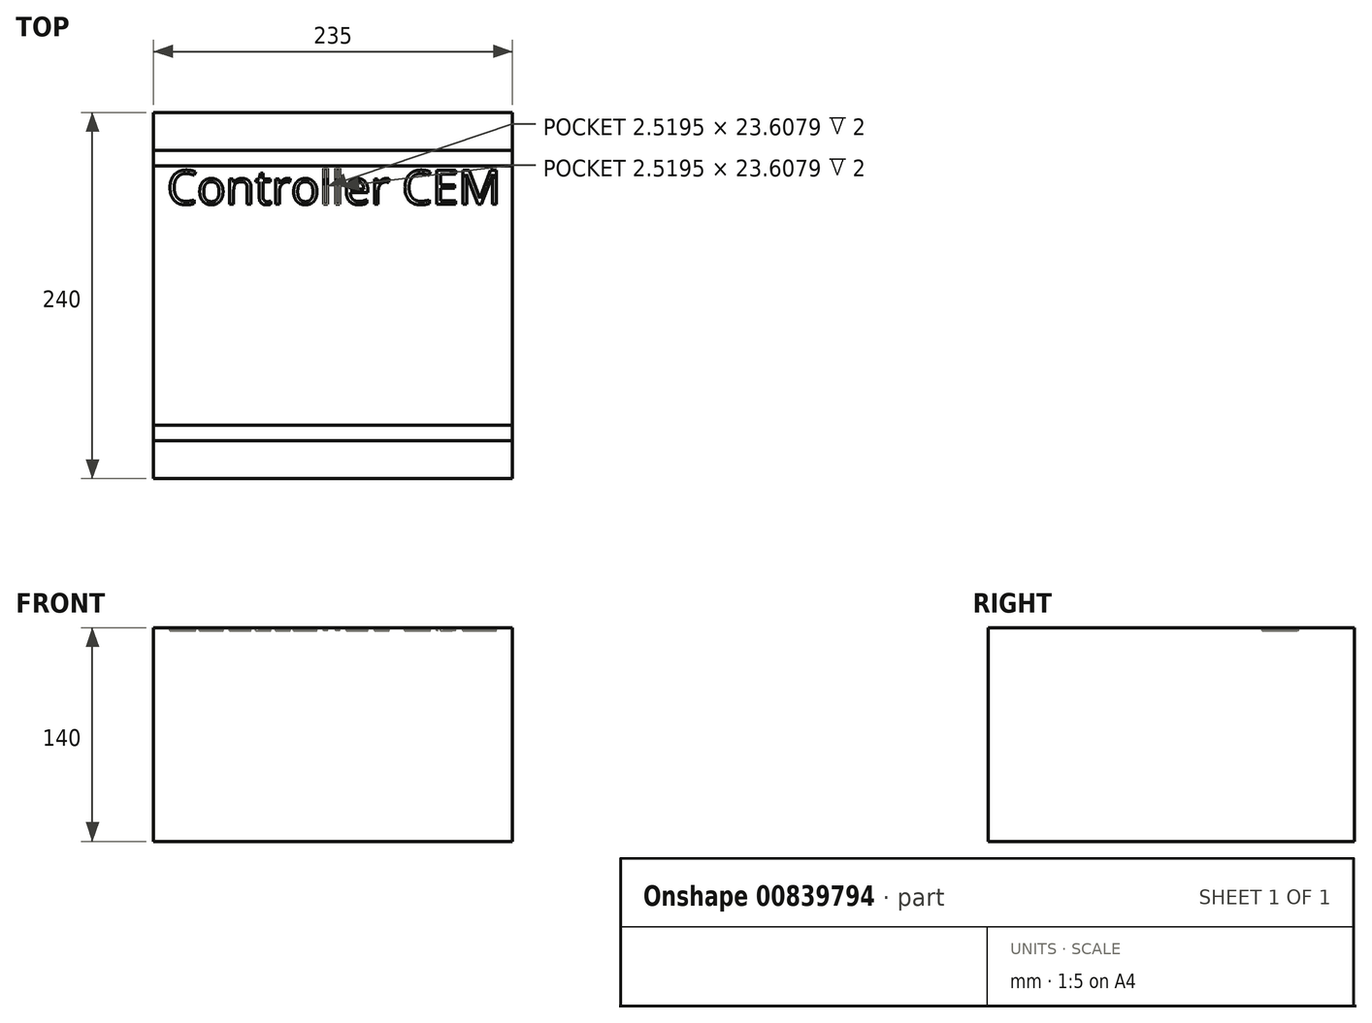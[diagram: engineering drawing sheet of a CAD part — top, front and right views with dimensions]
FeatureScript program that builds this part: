
annotation { "Feature Type Name" : "Feature", "Feature Type Description" : "" }
export const myFeature = defineFeature(function(context is Context, id is Id, definition is map)
    precondition{}
    {
        {
            var Q0;
            Q0=qCreatedBy(makeId("Top.planeOp"),FACE);
            var sketch = newSketch(context, id + "F0", { "sketchPlane" : qUnion([Q0])});
            skLineSegment(sketch, "E0.bottom", {"start": v(-117.5, 120) * mm, "end": v(117.5, 120) * mm});
            skLineSegment(sketch, "E0.top", {"start": v(-117.5, -120) * mm, "end": v(117.5, -120) * mm});
            skLineSegment(sketch, "E0.left", {"start": v(-117.5, 120) * mm, "end": v(-117.5, -120) * mm});
            skLineSegment(sketch, "E0.right", {"start": v(117.5, 120) * mm, "end": v(117.5, -120) * mm});
            skPoint(sketch, "E0.middle", {"position": v(0, 0) * mm});
            skSolve(sketch);
        }
        {
            var Q0;
            Q0 = qSketchRegion(id + "F0", true);
            extrude(context, id + "F1", {"entities" : qUnion([Q0]), "depth" : 140 * mm, "offsetDistance" : 25 * mm});
        }
        {
            var Q0;
            Q0=makeQuery(id+"F1.opExtrude","CAP_FACE",FACE,{"disambiguationData":[OSD([sQuery(id+"F0.wireOp",EDGE,"E0.bottom"),sQuery(id+"F0.wireOp",EDGE,"E0.top"),sQuery(id+"F0.wireOp",EDGE,"E0.left"),sQuery(id+"F0.wireOp",EDGE,"E0.right")])],"isStart":false});
            var sketch = newSketch(context, id + "F2", { "sketchPlane" : qUnion([Q0])});
            skText(sketch, "E1", { "text": "Controller CEM", "fontName": "OpenSans-Regular.ttf"});
            const initialGuessF2  = {"E1": [-0.10864, 0.05975, 1, 0, 0.02237]};
            skSetInitialGuess(sketch, initialGuessF2);
            skSolve(sketch);
        }
        {
            var Q0;
            Q0 = qSketchRegion(id + "F2", true);
            extrude(context, id + "F3", {"entities" : qUnion([Q0]), "operationType" : NewBodyOperationType.REMOVE, "oppositeDirection" : true, "depth" : 2 * mm, "offsetDistance" : 25 * mm});
        }
        {
            var Q0;
            {var subQ0=sQuery(id+"F0.wireOp",EDGE,"E0.top");var subQ1=sQuery(id+"F0.wireOp",EDGE,"E0.right");var subQ2=sQuery(id+"F0.wireOp",EDGE,"E0.bottom");var subQ3=sQuery(id+"F0.wireOp",EDGE,"E0.left");Q0=makeQuery(id+"F3.boolean.opBoolean","SPLIT",FACE,{"disambiguationData":[TD([makeQuery(id+"F1.opExtrude","SWEPT_FACE",FACE,{"disambiguationData":[OSD([subQ2])]})])],"derivedFrom":makeQuery(id+"F1.opExtrude","CAP_FACE",FACE,{"disambiguationData":[OSD([subQ2,subQ0,subQ3,subQ1])],"isStart":false})});}
            var sketch = newSketch(context, id + "F4", { "sketchPlane" : qUnion([Q0])});
            skLineSegment(sketch, "E2.bottom", {"start": v(-117.5, -95) * mm, "end": v(117.5, -95) * mm});
            skLineSegment(sketch, "E2.top", {"start": v(-117.5, -85) * mm, "end": v(117.5, -85) * mm});
            skLineSegment(sketch, "E2.left", {"start": v(-117.5, -95) * mm, "end": v(-117.5, -85) * mm});
            skLineSegment(sketch, "E2.right", {"start": v(117.5, -95) * mm, "end": v(117.5, -85) * mm});
            skLineSegment(sketch, "E3.MirrorCS", {"start": v(-117.5, 85) * mm, "end": v(117.5, 85) * mm});
            skLineSegment(sketch, "E4.MirrorCS", {"start": v(-117.5, 95) * mm, "end": v(117.5, 95) * mm});
            skLineSegment(sketch, "E5.MirrorCS", {"start": v(-117.5, 95) * mm, "end": v(-117.5, 85) * mm});
            skLineSegment(sketch, "E6.MirrorCS", {"start": v(117.5, 95) * mm, "end": v(117.5, 85) * mm});
            skSolve(sketch);
        }
        {
            var Q0;
            Q0 = qSketchRegion(id + "F4", true);
            extrude(context, id + "F5", {"entities" : qUnion([Q0]), "operationType" : NewBodyOperationType.REMOVE, "oppositeDirection" : true, "depth" : 0.1 * mm, "offsetDistance" : 25 * mm});
        }
    });
